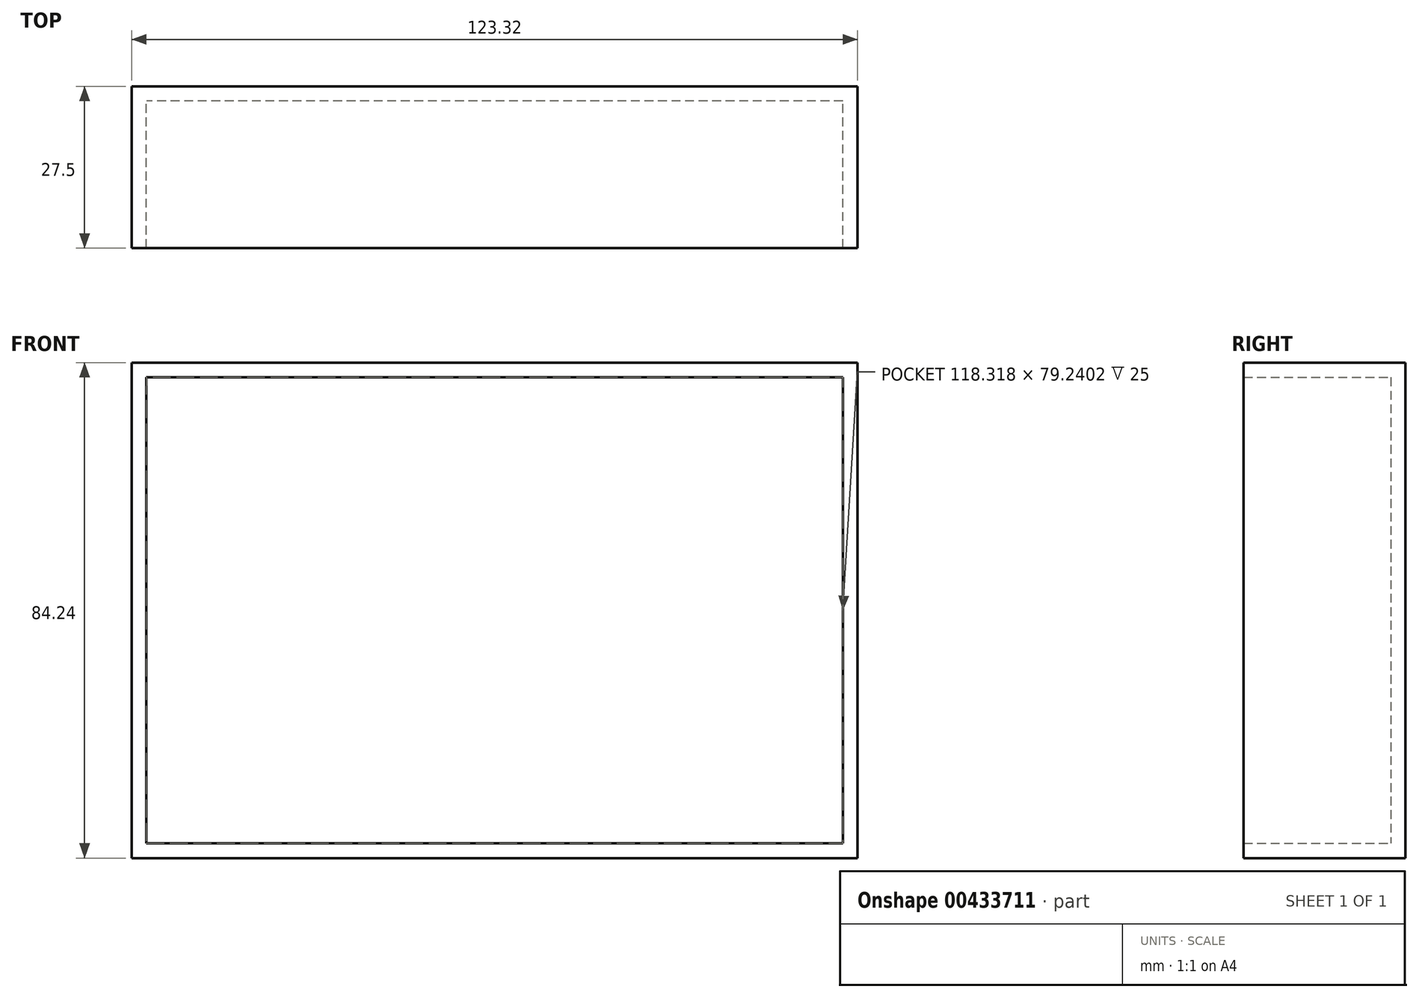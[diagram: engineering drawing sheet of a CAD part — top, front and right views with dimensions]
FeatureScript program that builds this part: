
annotation { "Feature Type Name" : "Feature", "Feature Type Description" : "" }
export const myFeature = defineFeature(function(context is Context, id is Id, definition is map)
    precondition{}
    {
        {
            var Q0;
            Q0=qCreatedBy(makeId("Front.planeOp"),FACE);
            var sketch = newSketch(context, id + "F0", { "sketchPlane" : qUnion([Q0])});
            skLineSegment(sketch, "E0.bottom", {"start": v(59.16, 39.62) * mm, "end": v(-59.16, 39.62) * mm});
            skLineSegment(sketch, "E0.top", {"start": v(59.16, -39.62) * mm, "end": v(-59.16, -39.62) * mm});
            skLineSegment(sketch, "E0.left", {"start": v(59.16, 39.62) * mm, "end": v(59.16, -39.62) * mm});
            skLineSegment(sketch, "E0.right", {"start": v(-59.16, 39.62) * mm, "end": v(-59.16, -39.62) * mm});
            skPoint(sketch, "E0.middle", {"position": v(0, 0) * mm});
            skSolve(sketch);
        }
        {
            var Q0;
            Q0=makeQuery(id+"F0.imprint","IMPRINT",FACE,{"disambiguationData":[TD([[makeQuery(id+"F0.imprint","IMPRINT",EDGE,{"derivedFrom":sQuery(id+"F0.wireOp",EDGE,"E0.bottom")}),1.0]])]});
            extrude(context, id + "F1", {"entities" : qUnion([Q0]), "depth" : 25 * mm});
        }
        {
            var Q0;
            Q0=makeQuery(id+"F1.opExtrude","CAP_FACE",FACE,{"disambiguationData":[OSD([sQuery(id+"F0.wireOp",EDGE,"E0.bottom"),sQuery(id+"F0.wireOp",EDGE,"E0.top"),sQuery(id+"F0.wireOp",EDGE,"E0.left"),sQuery(id+"F0.wireOp",EDGE,"E0.right")])],"isStart":false});
            shell(context, id + "F2", {"entities" : qUnion([Q0]), "thickness" : 2.5 * mm, "oppositeDirection" : true});
        }
    });
